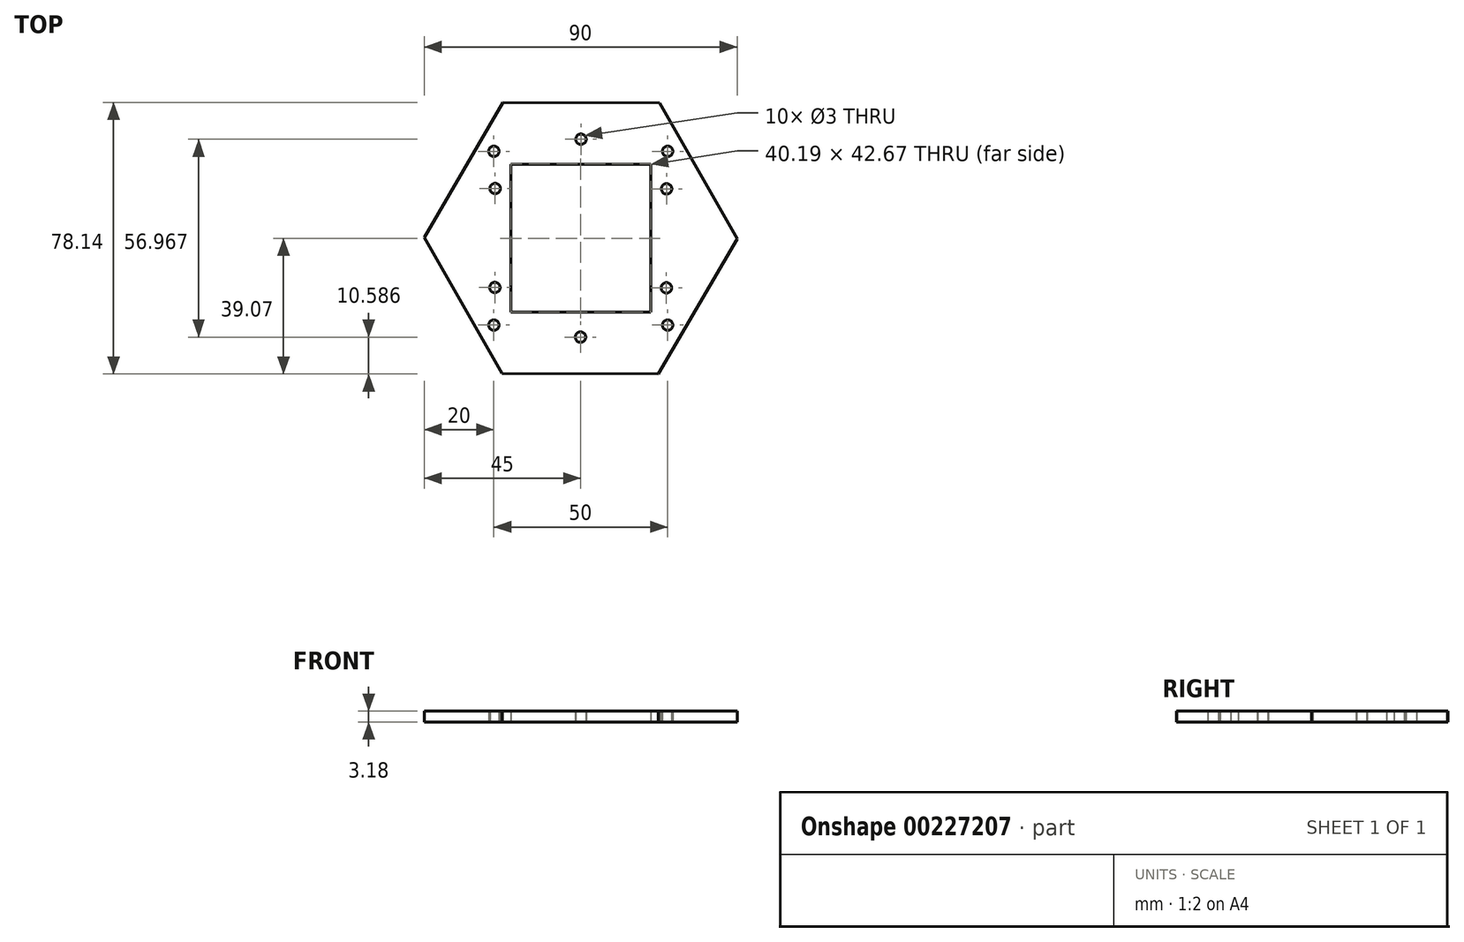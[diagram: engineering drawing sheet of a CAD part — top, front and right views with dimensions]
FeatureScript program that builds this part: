
annotation { "Feature Type Name" : "Feature", "Feature Type Description" : "" }
export const myFeature = defineFeature(function(context is Context, id is Id, definition is map)
    precondition{}
    {
        {
            var Q0;
            Q0=qCreatedBy(makeId("Top.planeOp"),FACE);
            var sketch = newSketch(context, id + "F0", { "sketchPlane" : qUnion([Q0])});
            skCircle(sketch, "E0.cCircle", {"center": v(0, 0) * mm, "radius": 45 * mm, "construction": true});
            skLineSegment(sketch, "E0.0", {"start": v(22.33, -39.07) * mm, "end": v(-22.67, -38.87) * mm});
            skLineSegment(sketch, "E0.1", {"start": v(-22.67, -38.87) * mm, "end": v(-45, 0.2) * mm});
            skLineSegment(sketch, "E0.2", {"start": v(-45, 0.2) * mm, "end": v(-22.33, 39.07) * mm});
            skLineSegment(sketch, "E0.3", {"start": v(-22.33, 39.07) * mm, "end": v(22.67, 38.87) * mm});
            skLineSegment(sketch, "E0.4", {"start": v(22.67, 38.87) * mm, "end": v(45, -0.2) * mm});
            skLineSegment(sketch, "E0.5", {"start": v(45, -0.2) * mm, "end": v(22.33, -39.07) * mm});
            skCircle(sketch, "E1.cCircle", {"center": v(0, 0) * mm, "radius": 28.48 * mm, "construction": true});
            skLineSegment(sketch, "E1.0", {"start": v(24.64, -14.3) * mm, "end": v(-0.06, -28.48) * mm, "construction": true});
            skLineSegment(sketch, "E1.1", {"start": v(-0.06, -28.48) * mm, "end": v(-24.7, -14.19) * mm, "construction": true});
            skLineSegment(sketch, "E1.2", {"start": v(-24.7, -14.19) * mm, "end": v(-24.64, 14.3) * mm, "construction": true});
            skLineSegment(sketch, "E1.3", {"start": v(-24.64, 14.3) * mm, "end": v(0.06, 28.48) * mm, "construction": true});
            skLineSegment(sketch, "E1.4", {"start": v(0.06, 28.48) * mm, "end": v(24.7, 14.19) * mm, "construction": true});
            skLineSegment(sketch, "E1.5", {"start": v(24.7, 14.19) * mm, "end": v(24.64, -14.3) * mm, "construction": true});
            skCircle(sketch, "E2", {"center": v(0.06, 28.48) * mm, "radius": 1.5 * mm});
            skCircle(sketch, "E3.1.0", {"center": v(-24.64, 14.3) * mm, "radius": 1.5 * mm});
            skCircle(sketch, "E3.2.0", {"center": v(-24.7, -14.19) * mm, "radius": 1.5 * mm});
            skCircle(sketch, "E3.3.0", {"center": v(-0.06, -28.48) * mm, "radius": 1.5 * mm});
            skCircle(sketch, "E3.4.0", {"center": v(24.64, -14.3) * mm, "radius": 1.5 * mm});
            skCircle(sketch, "E3.5.0", {"center": v(24.7, 14.19) * mm, "radius": 1.5 * mm});
            skLineSegment(sketch, "E4.bottom", {"start": v(25, -25) * mm, "end": v(-25, -25) * mm, "construction": true});
            skLineSegment(sketch, "E4.top", {"start": v(25, 25) * mm, "end": v(-25, 25) * mm, "construction": true});
            skLineSegment(sketch, "E4.left", {"start": v(25, -25) * mm, "end": v(25, 25) * mm, "construction": true});
            skLineSegment(sketch, "E4.right", {"start": v(-25, -25) * mm, "end": v(-25, 25) * mm, "construction": true});
            skCircle(sketch, "E5", {"center": v(-25, 25) * mm, "radius": 1.5 * mm});
            skCircle(sketch, "E6.1.0", {"center": v(-25, -25) * mm, "radius": 1.5 * mm});
            skCircle(sketch, "E6.2.0", {"center": v(25, -25) * mm, "radius": 1.5 * mm});
            skCircle(sketch, "E6.3.0", {"center": v(25, 25) * mm, "radius": 1.5 * mm});
            skLineSegment(sketch, "E7.bottom", {"start": v(-20.1, -21.34) * mm, "end": v(20.1, -21.34) * mm});
            skLineSegment(sketch, "E7.top", {"start": v(-20.1, 21.34) * mm, "end": v(20.1, 21.34) * mm});
            skLineSegment(sketch, "E7.left", {"start": v(-20.1, -21.34) * mm, "end": v(-20.1, 21.34) * mm});
            skLineSegment(sketch, "E7.right", {"start": v(20.1, -21.34) * mm, "end": v(20.1, 21.34) * mm});
            skPoint(sketch, "E7.cornerSnap0", {"position": v(-12.38, -21.34) * mm});
            skSolve(sketch);
        }
        {
            var Q0;
            Q0=makeQuery(id+"F0.imprint","IMPRINT",FACE,{"disambiguationData":[TD([[makeQuery(id+"F0.imprint","IMPRINT",EDGE,{"derivedFrom":sQuery(id+"F0.wireOp",EDGE,"E0.0")}),-1.0]])]});
            extrude(context, id + "F1", {"entities" : qUnion([Q0]), "depth" : 3.17 * mm});
        }
    });
